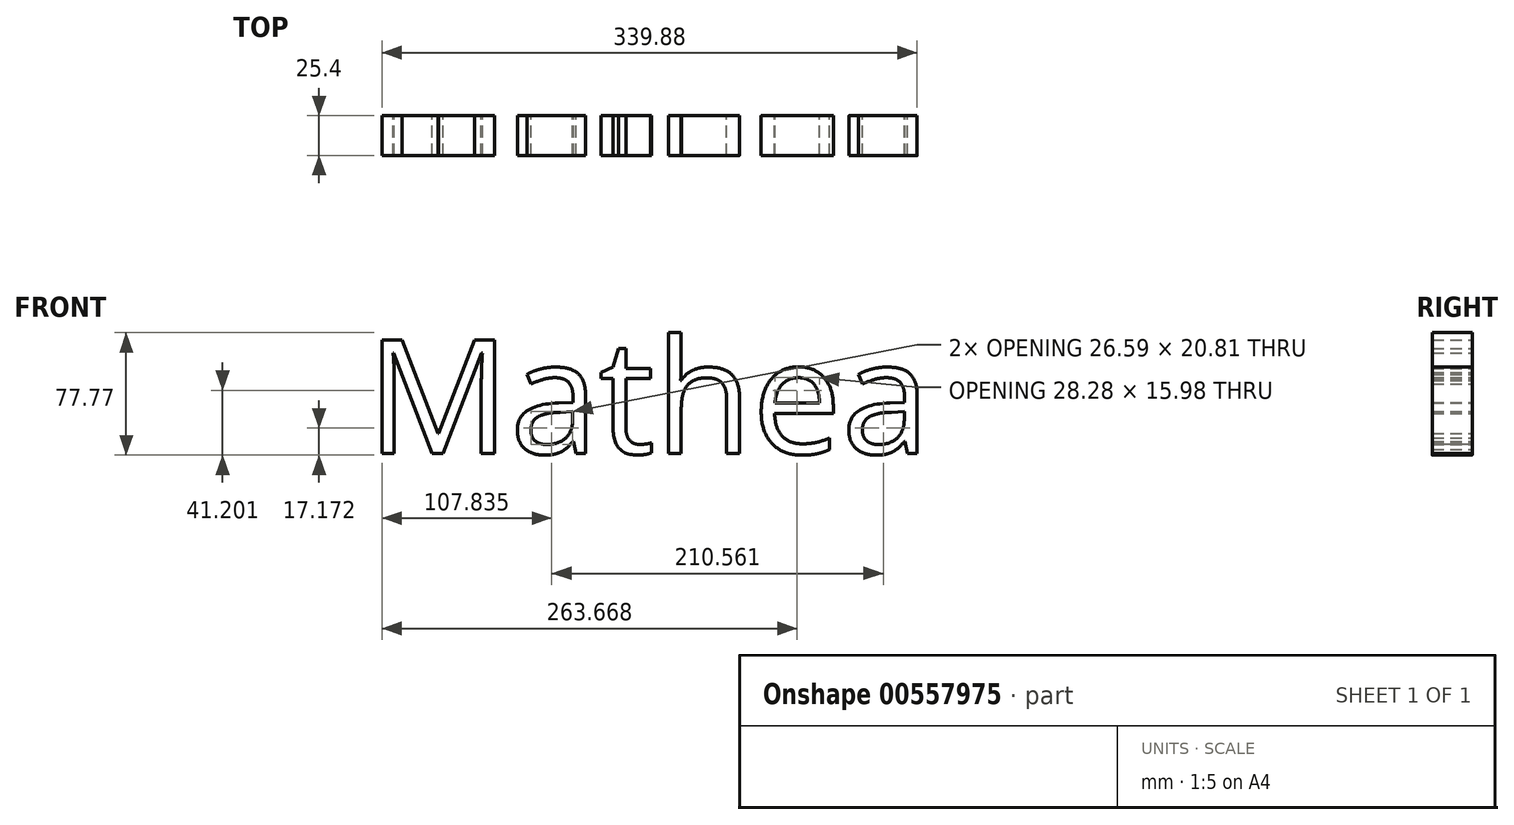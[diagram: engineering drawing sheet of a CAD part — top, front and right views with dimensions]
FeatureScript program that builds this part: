
annotation { "Feature Type Name" : "Feature", "Feature Type Description" : "" }
export const myFeature = defineFeature(function(context is Context, id is Id, definition is map)
    precondition{}
    {
        {
            var Q0;
            Q0=qCreatedBy(makeId("Front.planeOp"),FACE);
            var sketch = newSketch(context, id + "F0", { "sketchPlane" : qUnion([Q0])});
            skText(sketch, "E0", { "text": "Mathea", "fontName": "OpenSans-Regular.ttf"});
            const initialGuessF0  = {"E0": [-0.16193, -0.01829, 1, 0, 0.07275]};
            skSetInitialGuess(sketch, initialGuessF0);
            skSolve(sketch);
        }
        {
            var Q0;
            Q0 = qSketchRegion(id + "F0", true);
            extrude(context, id + "F1", {"entities" : qUnion([Q0]), "depth" : 25.4 * mm, "offsetDistance" : 25.4 * mm});
        }
    });
